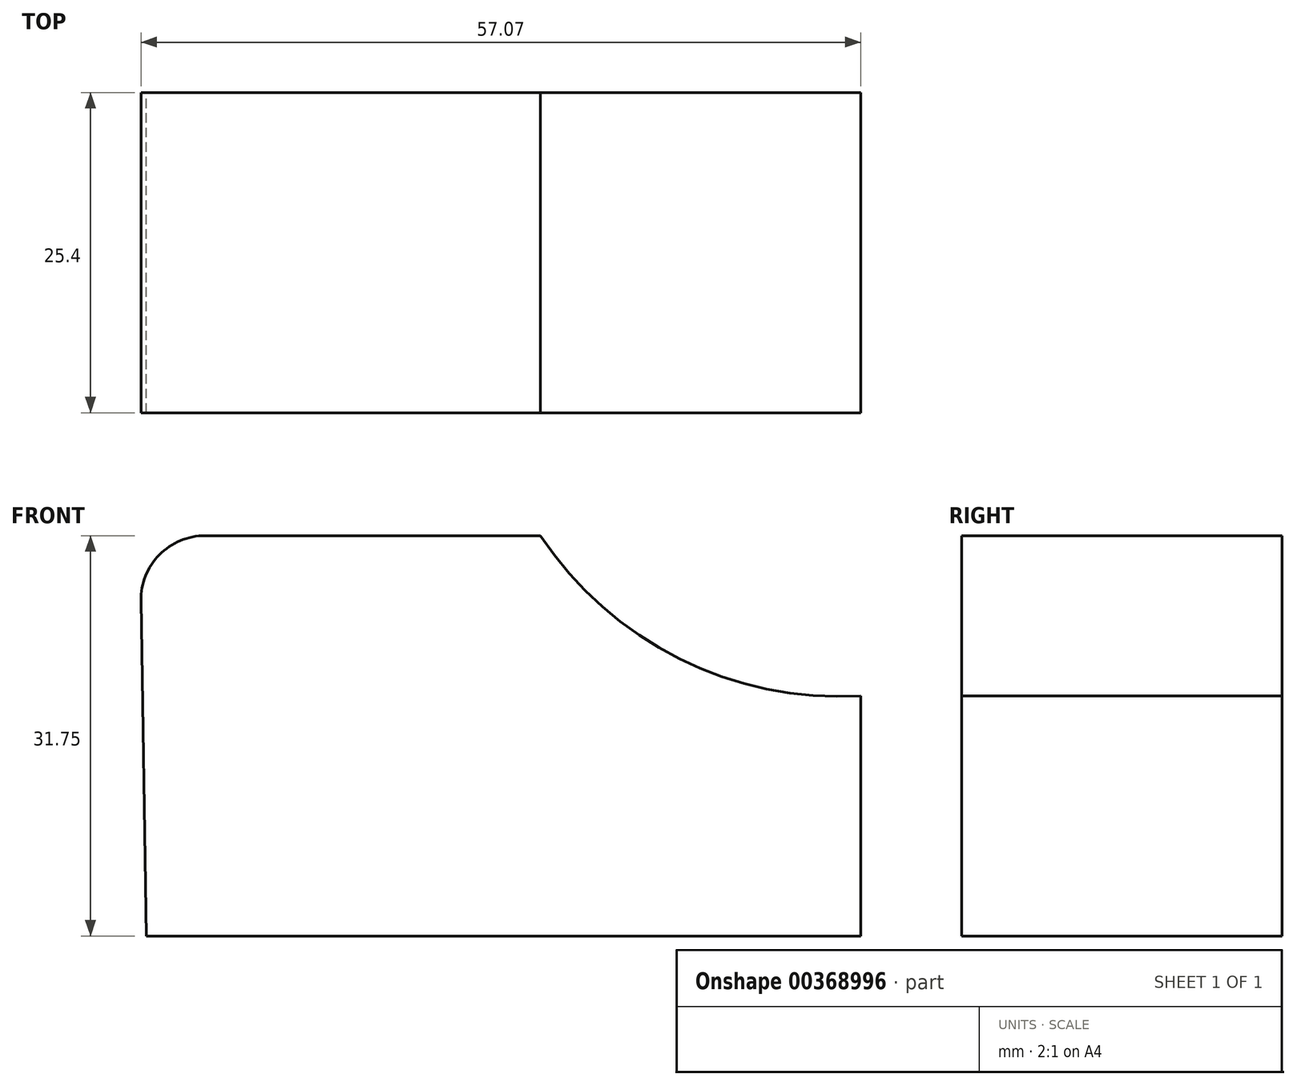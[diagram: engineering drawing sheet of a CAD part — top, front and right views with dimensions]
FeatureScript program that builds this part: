
annotation { "Feature Type Name" : "Feature", "Feature Type Description" : "" }
export const myFeature = defineFeature(function(context is Context, id is Id, definition is map)
    precondition{}
    {
        {
            var Q0;
            Q0=qCreatedBy(makeId("Front.planeOp"),FACE);
            var sketch = newSketch(context, id + "F0", { "sketchPlane" : qUnion([Q0])});
            skLineSegment(sketch, "E0", {"start": v(-45.07, 0) * mm, "end": v(11.58, 0) * mm});
            skLineSegment(sketch, "E1", {"start": v(11.58, 0) * mm, "end": v(11.58, 31.75) * mm});
            skLineSegment(sketch, "E2", {"start": v(11.58, 31.75) * mm, "end": v(-45.57, 31.75) * mm});
            skLineSegment(sketch, "E3", {"start": v(-45.57, 31.75) * mm, "end": v(-45.07, 0) * mm});
            skSolve(sketch);
        }
        {
            var Q0;
            Q0=makeQuery(id+"F0.imprint","IMPRINT",FACE,{"disambiguationData":[TD([[makeQuery(id+"F0.imprint","IMPRINT",EDGE,{"derivedFrom":sQuery(id+"F0.wireOp",EDGE,"E0")}),1.0]])]});
            extrude(context, id + "F1", {"entities" : qUnion([Q0]), "depth" : 25.4 * mm});
        }
        {
            var Q0;
            Q0=makeQuery(id+"F1.opExtrude","CAP_FACE",FACE,{"disambiguationData":[OSD([sQuery(id+"F0.wireOp",EDGE,"E0"),sQuery(id+"F0.wireOp",EDGE,"E1"),sQuery(id+"F0.wireOp",EDGE,"E2"),sQuery(id+"F0.wireOp",EDGE,"E3")])],"isStart":false});
            var sketch = newSketch(context, id + "F2", { "sketchPlane" : qUnion([Q0])});
            skArc(sketch, "E4", {"start": v(-13.82, 31.75) * mm, "mid": v(-2.82, 22) * mm, "end": v(11.58, 19.05) * mm});
            skSolve(sketch);
        }
        {
            var Q0;
            {var subQ0=sQuery(id+"F2.wireOp",EDGE,"E4");Q0=makeQuery(id+"F2.imprint","IMPRINT",FACE,{"disambiguationData":[TD([[makeQuery(id+"F2.imprint","IMPRINT",EDGE,{"derivedFrom":subQ0}),1.0]])]});}
            extrude(context, id + "F3", {"entities" : qUnion([Q0]), "operationType" : NewBodyOperationType.REMOVE, "oppositeDirection" : true, "depth" : 25.4 * mm});
        }
        {
            var Q0;
            Q0=makeQuery(id+"F1.opExtrude","SWEPT_EDGE",EDGE,{"disambiguationData":[OSD([sQuery(id+"F0.wireOp",EDGE,"E2"),sQuery(id+"F0.wireOp",EDGE,"E3")])]});
            fillet(context, id + "F4", {"entities" : qUnion([Q0]), "radius" : 5.08 * mm, "tangentPropagation" : true, "allowEdgeOverflow" : false});
        }
    });
